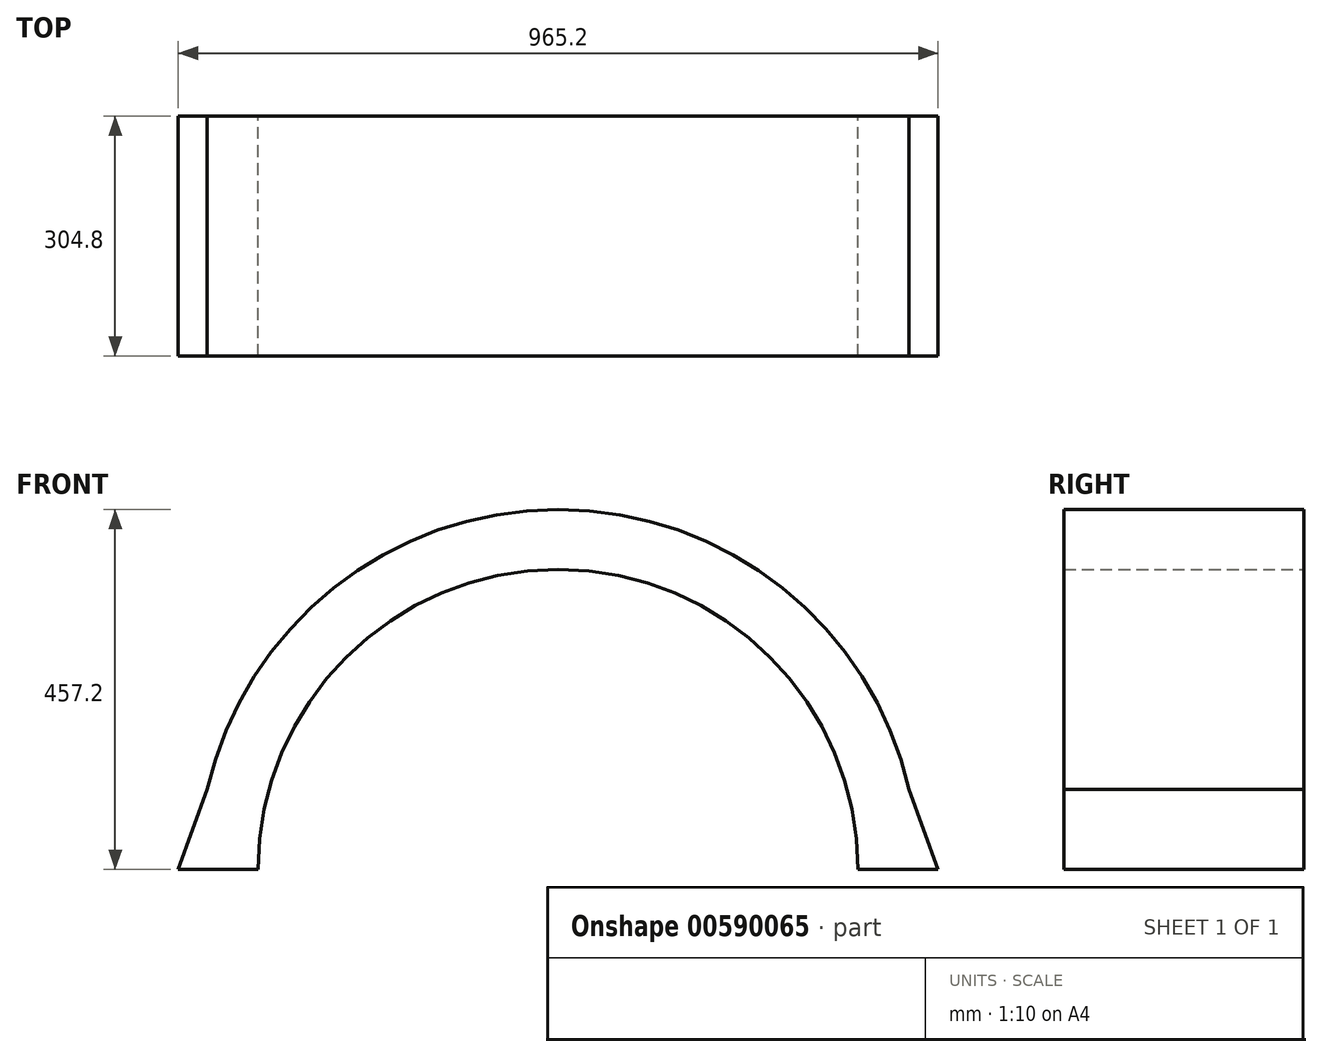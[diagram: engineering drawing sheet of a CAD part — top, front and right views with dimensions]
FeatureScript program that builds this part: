
annotation { "Feature Type Name" : "Feature", "Feature Type Description" : "" }
export const myFeature = defineFeature(function(context is Context, id is Id, definition is map)
    precondition{}
    {
        {
            var Q0;
            Q0=qCreatedBy(makeId("Front.planeOp"),FACE);
            var sketch = newSketch(context, id + "F0", { "sketchPlane" : qUnion([Q0])});
            skArc(sketch, "E0", {"start": v(381, 0) * mm, "mid": v(0, 381) * mm, "end": v(-381, 0) * mm});
            skArc(sketch, "E1.0", {"start": v(445.77, 101.6) * mm, "mid": v(0, 457.2) * mm, "end": v(-445.77, 101.6) * mm});
            skLineSegment(sketch, "E2", {"start": v(-457.2, 0) * mm, "end": v(-381, 0) * mm});
            skLineSegment(sketch, "E3.trimOffspring", {"start": v(381, 0) * mm, "end": v(457.2, 0) * mm});
            skLineSegment(sketch, "E4", {"start": v(-445.77, 101.6) * mm, "end": v(445.77, 101.6) * mm, "construction": true});
            skPoint(sketch, "E5.endSnap0", {"position": v(-419.1, 0) * mm});
            skLineSegment(sketch, "E6", {"start": v(457.2, 0) * mm, "end": v(482.6, 0) * mm});
            skLineSegment(sketch, "E7", {"start": v(-457.2, 0) * mm, "end": v(-482.6, 0) * mm});
            skLineSegment(sketch, "E8", {"start": v(-445.77, 101.6) * mm, "end": v(-482.6, 0) * mm});
            skLineSegment(sketch, "E9", {"start": v(445.77, 101.6) * mm, "end": v(482.6, 0) * mm});
            skSolve(sketch);
        }
        {
            var Q0;
            Q0 = qSketchRegion(id + "F0", true);
            extrude(context, id + "F1", {"entities" : qUnion([Q0]), "depth" : 304.8 * mm, "offsetDistance" : 25.4 * mm});
        }
    });
